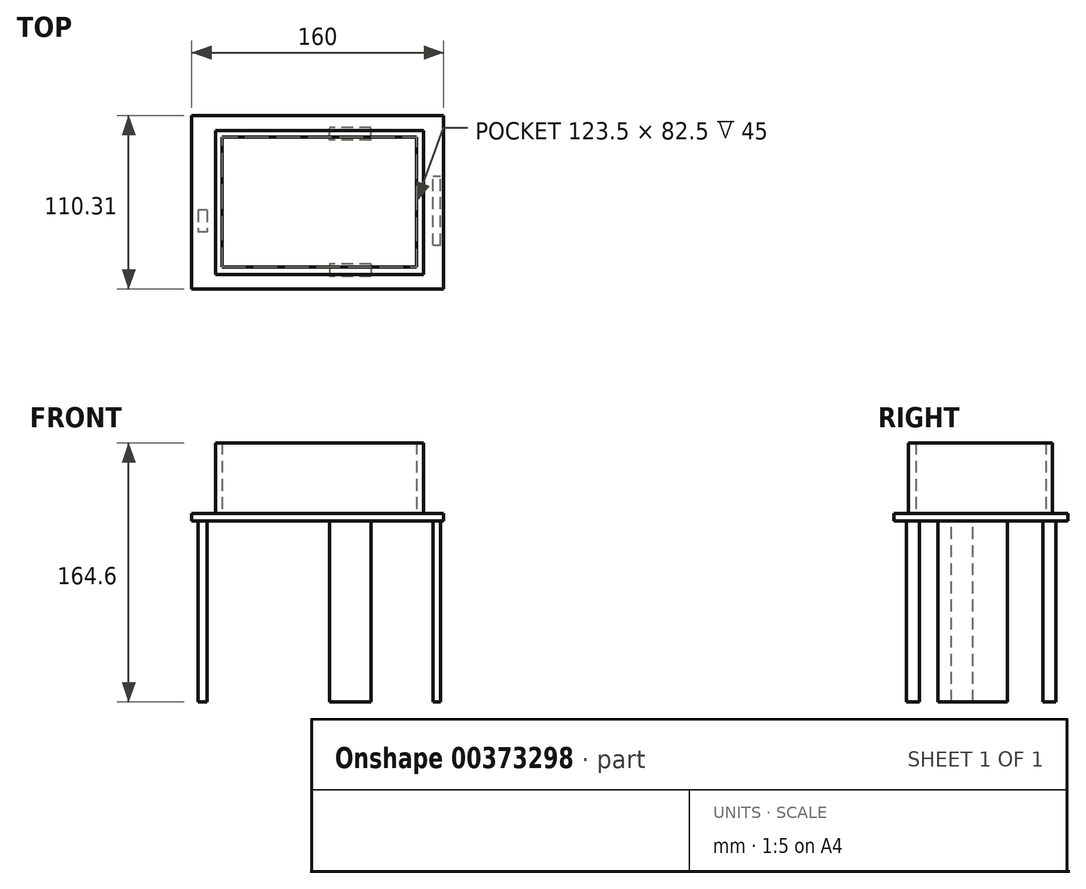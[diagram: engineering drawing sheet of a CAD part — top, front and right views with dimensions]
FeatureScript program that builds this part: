
annotation { "Feature Type Name" : "Feature", "Feature Type Description" : "" }
export const myFeature = defineFeature(function(context is Context, id is Id, definition is map)
    precondition{}
    {
        {
            var Q0;
            Q0=qCreatedBy(makeId("Top.planeOp"),FACE);
            var sketch = newSketch(context, id + "F0", { "sketchPlane" : qUnion([Q0])});
            skLineSegment(sketch, "E0.bottom", {"start": v(-62.57, 46.34) * mm, "end": v(60.93, 46.34) * mm});
            skLineSegment(sketch, "E0.top", {"start": v(-62.57, -36.16) * mm, "end": v(60.93, -36.16) * mm});
            skLineSegment(sketch, "E0.left", {"start": v(-62.57, 46.34) * mm, "end": v(-62.57, -36.16) * mm});
            skLineSegment(sketch, "E0.right", {"start": v(60.93, 46.34) * mm, "end": v(60.93, -36.16) * mm});
            skLineSegment(sketch, "E1.bottom", {"start": v(-66.65, 50.39) * mm, "end": v(65.53, 50.39) * mm});
            skLineSegment(sketch, "E1.top", {"start": v(-66.65, -41) * mm, "end": v(65.53, -41) * mm});
            skLineSegment(sketch, "E1.left", {"start": v(-66.65, 50.39) * mm, "end": v(-66.65, -41) * mm});
            skLineSegment(sketch, "E1.right", {"start": v(65.53, 50.39) * mm, "end": v(65.53, -41) * mm});
            skSolve(sketch);
        }
        {
            var Q0;
            Q0=makeQuery(id+"F0.imprint","IMPRINT",FACE,{"disambiguationData":[TD([[makeQuery(id+"F0.imprint","IMPRINT",EDGE,{"derivedFrom":sQuery(id+"F0.wireOp",EDGE,"E0.bottom")}),1.0]])]});
            extrude(context, id + "F1", {"entities" : qUnion([Q0]), "depth" : 45 * mm});
        }
        {
            var Q0;
            Q0=qCreatedBy(makeId("Top.planeOp"),FACE);
            var sketch = newSketch(context, id + "F2", { "sketchPlane" : qUnion([Q0])});
            skLineSegment(sketch, "E2.bottom", {"start": v(-81.75, 60.04) * mm, "end": v(78.25, 60.04) * mm});
            skLineSegment(sketch, "E2.top", {"start": v(-81.75, -50.27) * mm, "end": v(78.25, -50.27) * mm});
            skLineSegment(sketch, "E2.left", {"start": v(-81.75, 60.04) * mm, "end": v(-81.75, -50.27) * mm});
            skLineSegment(sketch, "E2.right", {"start": v(78.25, 60.04) * mm, "end": v(78.25, -50.27) * mm});
            skSolve(sketch);
        }
        {
            var Q0;
            Q0=makeQuery(id+"F2.imprint","IMPRINT",FACE,{"disambiguationData":[TD([[makeQuery(id+"F2.imprint","IMPRINT",EDGE,{"derivedFrom":sQuery(id+"F2.wireOp",EDGE,"E2.bottom")}),-1.0]])]});
            extrude(context, id + "F3", {"entities" : qUnion([Q0]), "operationType" : NewBodyOperationType.ADD, "oppositeDirection" : true, "depth" : 4.6 * mm});
        }
        {
            var Q0;
            Q0=makeQuery(id+"F3.opExtrude","CAP_FACE",FACE,{"disambiguationData":[OSD([sQuery(id+"F2.wireOp",EDGE,"E2.bottom"),sQuery(id+"F2.wireOp",EDGE,"E2.top"),sQuery(id+"F2.wireOp",EDGE,"E2.left"),sQuery(id+"F2.wireOp",EDGE,"E2.right")])],"isStart":false});
            var sketch = newSketch(context, id + "F4", { "sketchPlane" : qUnion([Q0])});
            skLineSegment(sketch, "E3.bottom", {"start": v(32.27, 34.1) * mm, "end": v(5.87, 34.1) * mm});
            skLineSegment(sketch, "E3.top", {"start": v(32.27, 42.23) * mm, "end": v(5.87, 42.23) * mm});
            skLineSegment(sketch, "E3.left", {"start": v(32.27, 34.1) * mm, "end": v(32.27, 42.23) * mm});
            skLineSegment(sketch, "E3.right", {"start": v(5.87, 34.1) * mm, "end": v(5.87, 42.23) * mm});
            skPoint(sketch, "E4.oppositeSnap0", {"position": v(5.87, 38.17) * mm});
            skLineSegment(sketch, "E4.bottom", {"start": v(32.27, -44.4) * mm, "end": v(5.87, -44.4) * mm});
            skLineSegment(sketch, "E4.top", {"start": v(32.27, -52.51) * mm, "end": v(5.87, -52.51) * mm});
            skLineSegment(sketch, "E4.left", {"start": v(32.27, -44.4) * mm, "end": v(32.27, -52.51) * mm});
            skLineSegment(sketch, "E4.right", {"start": v(5.87, -44.4) * mm, "end": v(5.87, -52.51) * mm});
            skSolve(sketch);
        }
        {
            var Q0;
            Q0=makeQuery(id+"F4.imprint","IMPRINT",FACE,{"disambiguationData":[TD([[makeQuery(id+"F4.imprint","IMPRINT",EDGE,{"derivedFrom":sQuery(id+"F4.wireOp",EDGE,"E3.bottom")}),-1.0]])]});
            var Q1;
            Q1=makeQuery(id+"F4.imprint","IMPRINT",FACE,{"disambiguationData":[TD([[makeQuery(id+"F4.imprint","IMPRINT",EDGE,{"derivedFrom":sQuery(id+"F4.wireOp",EDGE,"E4.bottom")}),1.0]])]});
            extrude(context, id + "F5", {"entities" : qUnion([Q0, Q1]), "operationType" : NewBodyOperationType.ADD, "depth" : 115 * mm});
        }
        {
            var Q0;
            Q0=makeQuery(id+"F3.opExtrude","CAP_FACE",FACE,{"disambiguationData":[OSD([sQuery(id+"F2.wireOp",EDGE,"E2.bottom"),sQuery(id+"F2.wireOp",EDGE,"E2.top"),sQuery(id+"F2.wireOp",EDGE,"E2.left"),sQuery(id+"F2.wireOp",EDGE,"E2.right")])],"isStart":false});
            var sketch = newSketch(context, id + "F6", { "sketchPlane" : qUnion([Q0])});
            skLineSegment(sketch, "E5", {"start": v(65.47, 57.54) * mm, "end": v(-78.2, 57.54) * mm});
            skLineSegment(sketch, "E6.bottom", {"start": v(71.37, 22.32) * mm, "end": v(76.17, 22.32) * mm});
            skLineSegment(sketch, "E6.top", {"start": v(71.37, -21.76) * mm, "end": v(76.17, -21.76) * mm});
            skLineSegment(sketch, "E6.left", {"start": v(71.37, 22.32) * mm, "end": v(71.37, -21.76) * mm});
            skLineSegment(sketch, "E6.right", {"start": v(76.17, 22.32) * mm, "end": v(76.17, -21.76) * mm});
            skSolve(sketch);
        }
        {
            var Q0;
            Q0=makeQuery(id+"F6.imprint","IMPRINT",FACE,{"disambiguationData":[TD([[makeQuery(id+"F6.imprint","IMPRINT",EDGE,{"derivedFrom":sQuery(id+"F6.wireOp",EDGE,"E6.bottom")}),-1.0]])]});
            var Q1;
            Q1 = qSketchRegion(id + "F4", true);
            extrude(context, id + "F7", {"entities" : qUnion([Q0, Q1]), "operationType" : NewBodyOperationType.ADD, "depth" : 115 * mm});
        }
        {
            var Q0;
            Q0=makeQuery(id+"F3.opExtrude","CAP_FACE",FACE,{"disambiguationData":[OSD([sQuery(id+"F2.wireOp",EDGE,"E2.bottom"),sQuery(id+"F2.wireOp",EDGE,"E2.top"),sQuery(id+"F2.wireOp",EDGE,"E2.left"),sQuery(id+"F2.wireOp",EDGE,"E2.right")])],"isStart":false});
            var sketch = newSketch(context, id + "F8", { "sketchPlane" : qUnion([Q0])});
            skLineSegment(sketch, "E7", {"start": v(71.37, 57.17) * mm, "end": v(-72.13, 57.17) * mm});
            skLineSegment(sketch, "E8.bottom", {"start": v(-72.13, 0) * mm, "end": v(-77.64, 0) * mm});
            skLineSegment(sketch, "E8.top", {"start": v(-72.13, 13.83) * mm, "end": v(-77.64, 13.83) * mm});
            skLineSegment(sketch, "E8.left", {"start": v(-72.13, 0) * mm, "end": v(-72.13, 13.83) * mm});
            skLineSegment(sketch, "E8.right", {"start": v(-77.64, 0) * mm, "end": v(-77.64, 13.83) * mm});
            skSolve(sketch);
        }
        {
            var Q0;
            Q0=makeQuery(id+"F8.imprint","IMPRINT",FACE,{"disambiguationData":[TD([[makeQuery(id+"F8.imprint","IMPRINT",EDGE,{"derivedFrom":sQuery(id+"F8.wireOp",EDGE,"E8.bottom")}),-1.0]])]});
            extrude(context, id + "F9", {"entities" : qUnion([Q0]), "operationType" : NewBodyOperationType.ADD, "depth" : 115 * mm});
        }
        {
            var Q0;
            Q0=makeQuery(id+"F3.opExtrude","CAP_FACE",FACE,{"disambiguationData":[OSD([sQuery(id+"F2.wireOp",EDGE,"E2.bottom"),sQuery(id+"F2.wireOp",EDGE,"E2.top"),sQuery(id+"F2.wireOp",EDGE,"E2.left"),sQuery(id+"F2.wireOp",EDGE,"E2.right")])],"isStart":false});
            var sketch = newSketch(context, id + "F10", { "sketchPlane" : qUnion([Q0])});
            skCircle(sketch, "E9", {"center": v(-66.63, 23) * mm, "radius": 2 * mm});
            skLineSegment(sketch, "E10", {"start": v(-84.56, 23) * mm, "end": v(-84.56, 0) * mm});
            skLineSegment(sketch, "E11", {"start": v(-84.56, 0) * mm, "end": v(-84.56, -23) * mm});
            skCircle(sketch, "E12", {"center": v(-66.3, -23.32) * mm, "radius": 2 * mm});
            skSolve(sketch);
        }
        {
            var Q0;
            Q0=sQuery(id+"F10.wireOp",EDGE,"E12");
            var Q1;
            Q1=sQuery(id+"F10.wireOp",EDGE,"E9");
            extrude(context, id + "F11", {"bodyType" : ToolBodyType.SURFACE, "surfaceEntities" : qUnion([Q0, Q1]), "depth" : 115 * mm});
        }
    });
